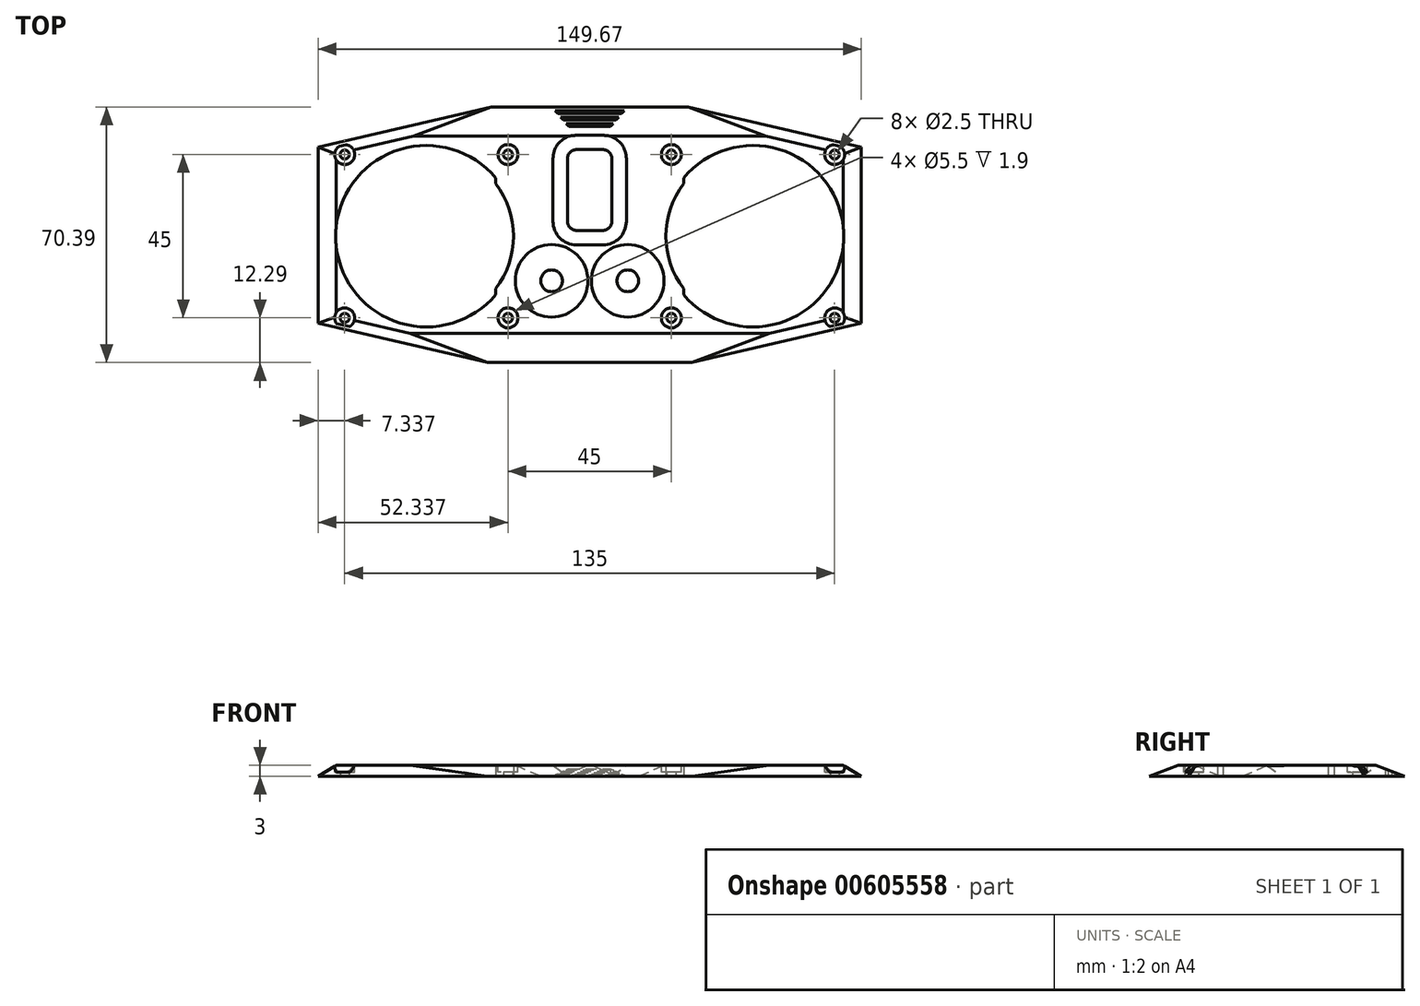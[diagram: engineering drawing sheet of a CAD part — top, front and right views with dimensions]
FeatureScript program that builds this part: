
annotation { "Feature Type Name" : "Feature", "Feature Type Description" : "" }
export const myFeature = defineFeature(function(context is Context, id is Id, definition is map)
    precondition{}
    {
        {
            var Q0;
            Q0=qCreatedBy(makeId("Top.planeOp"),FACE);
            var sketch = newSketch(context, id + "F0", { "sketchPlane" : qUnion([Q0])});
            skArc(sketch, "E0.0", {"start": v(-27.05, 29.93) * mm, "mid": v(-71.2, 13.86) * mm, "end": v(-27.05, -2.2) * mm});
            skArc(sketch, "E0.1", {"start": v(-27.05, -0.6) * mm, "mid": v(-22.2, 13.86) * mm, "end": v(-27.05, 28.32) * mm});
            skLineSegment(sketch, "E0.2", {"start": v(-27.05, -2.2) * mm, "end": v(-27.05, -0.6) * mm});
            skLineSegment(sketch, "E0.3", {"start": v(-27.05, 29.93) * mm, "end": v(-27.05, 28.32) * mm});
            skCircle(sketch, "E0.4", {"center": v(-23.7, 36.36) * mm, "radius": 1.25 * mm});
            skCircle(sketch, "E0.5", {"center": v(-68.7, 36.36) * mm, "radius": 1.25 * mm});
            skLineSegment(sketch, "E0.6", {"start": v(-77.2, 39.39) * mm, "end": v(-28.53, 50.62) * mm, "construction": true});
            skLineSegment(sketch, "E0.7", {"start": v(-77.2, 39.39) * mm, "end": v(-77.2, -45.78) * mm, "construction": true});
            skLineSegment(sketch, "E0.8", {"start": v(-28.53, 50.62) * mm, "end": v(26.12, 50.62) * mm, "construction": true});
            skLineSegment(sketch, "E0.9", {"start": v(74.8, 39.39) * mm, "end": v(26.12, 50.62) * mm, "construction": true});
            skLineSegment(sketch, "E0.10", {"start": v(-12.2, 50.26) * mm, "end": v(9.8, 50.26) * mm, "construction": true});
            skLineSegment(sketch, "E0.11", {"start": v(-11.4, 49.46) * mm, "end": v(9, 49.46) * mm, "construction": true});
            skLineSegment(sketch, "E0.12", {"start": v(8.3, 48.46) * mm, "end": v(-10.7, 48.46) * mm});
            skLineSegment(sketch, "E0.13", {"start": v(7.5, 47.66) * mm, "end": v(-9.9, 47.66) * mm});
            skLineSegment(sketch, "E0.14", {"start": v(6.8, 46.66) * mm, "end": v(-9.2, 46.66) * mm});
            skLineSegment(sketch, "E0.15", {"start": v(6, 45.86) * mm, "end": v(-8.4, 45.86) * mm});
            skLineSegment(sketch, "E0.16", {"start": v(5.3, 44.86) * mm, "end": v(-7.7, 44.86) * mm});
            skLineSegment(sketch, "E0.17", {"start": v(4.5, 44.06) * mm, "end": v(-6.9, 44.06) * mm});
            skLineSegment(sketch, "E0.18", {"start": v(-5.3, 35.25) * mm, "end": v(-5.3, 17.95) * mm, "construction": true});
            skLineSegment(sketch, "E0.19", {"start": v(2.4, 35.75) * mm, "end": v(-4.8, 35.75) * mm, "construction": true});
            skLineSegment(sketch, "E0.20", {"start": v(2.9, 35.25) * mm, "end": v(2.9, 17.95) * mm, "construction": true});
            skLineSegment(sketch, "E0.21", {"start": v(2.4, 17.45) * mm, "end": v(-4.8, 17.45) * mm, "construction": true});
            skArc(sketch, "E0.22", {"start": v(-4.8, 17.45) * mm, "mid": v(-5.16, 17.6) * mm, "end": v(-5.3, 17.95) * mm, "construction": true});
            skArc(sketch, "E0.23", {"start": v(2.9, 17.95) * mm, "mid": v(2.75, 17.6) * mm, "end": v(2.4, 17.45) * mm, "construction": true});
            skArc(sketch, "E0.24", {"start": v(2.4, 35.75) * mm, "mid": v(2.75, 35.6) * mm, "end": v(2.9, 35.25) * mm, "construction": true});
            skArc(sketch, "E0.25", {"start": v(-5.3, 35.25) * mm, "mid": v(-5.16, 35.6) * mm, "end": v(-4.8, 35.75) * mm, "construction": true});
            skCircle(sketch, "E0.26", {"center": v(21.3, 36.36) * mm, "radius": 1.25 * mm});
            skCircle(sketch, "E0.27", {"center": v(66.3, 36.36) * mm, "radius": 1.25 * mm});
            skCircle(sketch, "E0.28", {"center": v(66.3, -8.64) * mm, "radius": 1.25 * mm});
            skCircle(sketch, "E0.29", {"center": v(21.3, -8.64) * mm, "radius": 1.25 * mm});
            skArc(sketch, "E0.30", {"start": v(24.64, -2.2) * mm, "mid": v(68.8, 13.86) * mm, "end": v(24.64, 29.93) * mm});
            skArc(sketch, "E0.31", {"start": v(24.64, 28.32) * mm, "mid": v(19.8, 13.86) * mm, "end": v(24.64, -0.6) * mm});
            skLineSegment(sketch, "E0.32", {"start": v(74.8, -45.78) * mm, "end": v(74.8, 39.39) * mm, "construction": true});
            skLineSegment(sketch, "E0.33", {"start": v(24.64, -2.2) * mm, "end": v(24.64, -0.6) * mm});
            skLineSegment(sketch, "E0.34", {"start": v(24.64, 29.93) * mm, "end": v(24.64, 28.32) * mm});
            skLineSegment(sketch, "E0.35", {"start": v(13.5, 10.27) * mm, "end": v(5.1, 10.27) * mm, "construction": true});
            skLineSegment(sketch, "E0.36", {"start": v(13.5, 5.77) * mm, "end": v(13.5, 10.27) * mm, "construction": true});
            skLineSegment(sketch, "E0.37", {"start": v(18, 5.77) * mm, "end": v(13.5, 5.77) * mm, "construction": true});
            skLineSegment(sketch, "E0.38", {"start": v(18, -2.63) * mm, "end": v(18, 5.77) * mm, "construction": true});
            skLineSegment(sketch, "E0.39", {"start": v(13.5, -2.63) * mm, "end": v(18, -2.63) * mm, "construction": true});
            skLineSegment(sketch, "E0.40", {"start": v(13.5, -7.13) * mm, "end": v(13.5, -2.63) * mm, "construction": true});
            skLineSegment(sketch, "E0.41", {"start": v(13.5, -7.13) * mm, "end": v(5.1, -7.13) * mm, "construction": true});
            skLineSegment(sketch, "E0.42", {"start": v(5.1, -7.13) * mm, "end": v(5.1, -2.63) * mm, "construction": true});
            skLineSegment(sketch, "E0.43", {"start": v(0.6, -2.63) * mm, "end": v(5.1, -2.63) * mm, "construction": true});
            skLineSegment(sketch, "E0.44", {"start": v(0.6, -2.63) * mm, "end": v(0.6, 5.77) * mm, "construction": true});
            skLineSegment(sketch, "E0.45", {"start": v(5.1, 5.77) * mm, "end": v(0.6, 5.77) * mm, "construction": true});
            skLineSegment(sketch, "E0.46", {"start": v(5.1, 5.77) * mm, "end": v(5.1, 10.27) * mm, "construction": true});
            skLineSegment(sketch, "E0.47", {"start": v(-3, -2.63) * mm, "end": v(-3, 5.77) * mm, "construction": true});
            skLineSegment(sketch, "E0.48", {"start": v(-7.5, 5.77) * mm, "end": v(-3, 5.77) * mm, "construction": true});
            skLineSegment(sketch, "E0.49", {"start": v(-7.5, 5.77) * mm, "end": v(-7.5, 10.27) * mm, "construction": true});
            skLineSegment(sketch, "E0.50", {"start": v(-15.9, 10.27) * mm, "end": v(-7.5, 10.27) * mm, "construction": true});
            skLineSegment(sketch, "E0.51", {"start": v(-15.9, 5.77) * mm, "end": v(-15.9, 10.27) * mm, "construction": true});
            skLineSegment(sketch, "E0.52", {"start": v(-20.4, 5.77) * mm, "end": v(-15.9, 5.77) * mm, "construction": true});
            skLineSegment(sketch, "E0.53", {"start": v(-20.4, -2.63) * mm, "end": v(-20.4, 5.77) * mm, "construction": true});
            skLineSegment(sketch, "E0.54", {"start": v(-15.9, -2.63) * mm, "end": v(-20.4, -2.63) * mm, "construction": true});
            skLineSegment(sketch, "E0.55", {"start": v(-15.9, -7.13) * mm, "end": v(-15.9, -2.63) * mm, "construction": true});
            skLineSegment(sketch, "E0.56", {"start": v(-15.9, -7.13) * mm, "end": v(-7.5, -7.13) * mm, "construction": true});
            skLineSegment(sketch, "E0.57", {"start": v(-7.5, -7.13) * mm, "end": v(-7.5, -2.63) * mm, "construction": true});
            skLineSegment(sketch, "E0.58", {"start": v(-3, -2.63) * mm, "end": v(-7.5, -2.63) * mm, "construction": true});
            skCircle(sketch, "E0.59", {"center": v(-23.7, -8.64) * mm, "radius": 1.25 * mm});
            skCircle(sketch, "E0.60", {"center": v(-53.22, -28.82) * mm, "radius": 4.05 * mm, "construction": true});
            skCircle(sketch, "E0.61", {"center": v(-53.22, -42.82) * mm, "radius": 4.05 * mm, "construction": true});
            skLineSegment(sketch, "E0.62", {"start": v(-73.07, -50.7) * mm, "end": v(-43.77, -55.87) * mm, "construction": true});
            skArc(sketch, "E0.63", {"start": v(-77.2, -45.78) * mm, "mid": v(-76.03, -48.99) * mm, "end": v(-73.07, -50.7) * mm, "construction": true});
            skLineSegment(sketch, "E0.64", {"start": v(-43.77, -55.87) * mm, "end": v(41.36, -55.87) * mm, "construction": true});
            skLineSegment(sketch, "E0.65", {"start": v(41.36, -55.87) * mm, "end": v(70.67, -50.7) * mm, "construction": true});
            skCircle(sketch, "E0.66", {"center": v(53.62, -34.26) * mm, "radius": 16.25 * mm, "construction": true});
            skArc(sketch, "E0.67", {"start": v(70.67, -50.7) * mm, "mid": v(73.63, -48.99) * mm, "end": v(74.8, -45.78) * mm, "construction": true});
            skLineSegment(sketch, "E0.68", {"start": v(-29.45, -20.93) * mm, "end": v(27.05, -20.93) * mm});
            skLineSegment(sketch, "E0.69", {"start": v(27.05, -54.93) * mm, "end": v(27.05, -20.93) * mm, "construction": true});
            skLineSegment(sketch, "E0.70", {"start": v(-29.45, -54.93) * mm, "end": v(-29.45, -20.93) * mm, "construction": true});
            skLineSegment(sketch, "E0.71", {"start": v(-29.45, -54.93) * mm, "end": v(27.05, -54.93) * mm, "construction": true});
            skCircle(sketch, "E0.72", {"center": v(-68.7, -8.64) * mm, "radius": 1.25 * mm});
            skLineSegment(sketch, "E1", {"start": v(-1.2, 35.75) * mm, "end": v(-1.2, 17.45) * mm, "construction": true});
            skLineSegment(sketch, "E2", {"start": v(-5.3, 26.6) * mm, "end": v(2.9, 26.6) * mm, "construction": true});
            skLineSegment(sketch, "E3", {"start": v(-11.7, 10.27) * mm, "end": v(-11.7, -7.13) * mm, "construction": true});
            skLineSegment(sketch, "E4", {"start": v(-20.4, 1.57) * mm, "end": v(-3, 1.57) * mm, "construction": true});
            skLineSegment(sketch, "E5", {"start": v(9.3, 10.27) * mm, "end": v(9.3, -7.13) * mm, "construction": true});
            skLineSegment(sketch, "E6", {"start": v(0.6, 1.57) * mm, "end": v(18, 1.57) * mm, "construction": true});
            skCircle(sketch, "E7", {"center": v(-11.7, 1.57) * mm, "radius": 3 * mm});
            skCircle(sketch, "E8", {"center": v(9.3, 1.57) * mm, "radius": 3 * mm});
            skLineSegment(sketch, "E9", {"start": v(-12.2, 50.26) * mm, "end": v(-11.4, 49.46) * mm, "construction": true});
            skLineSegment(sketch, "E10", {"start": v(-10.7, 48.46) * mm, "end": v(-9.9, 47.66) * mm});
            skLineSegment(sketch, "E11", {"start": v(-9.2, 46.66) * mm, "end": v(-8.4, 45.86) * mm});
            skLineSegment(sketch, "E12", {"start": v(-7.7, 44.86) * mm, "end": v(-6.9, 44.06) * mm});
            skLineSegment(sketch, "E13", {"start": v(9.8, 50.26) * mm, "end": v(9, 49.46) * mm, "construction": true});
            skLineSegment(sketch, "E14", {"start": v(8.3, 48.46) * mm, "end": v(7.5, 47.66) * mm});
            skLineSegment(sketch, "E15", {"start": v(6.8, 46.66) * mm, "end": v(6, 45.86) * mm});
            skLineSegment(sketch, "E16", {"start": v(5.3, 44.86) * mm, "end": v(4.5, 44.06) * mm});
            skArc(sketch, "E17.0", {"start": v(4.9, 17.95) * mm, "mid": v(4.17, 16.19) * mm, "end": v(2.4, 15.45) * mm});
            skLineSegment(sketch, "E17.1", {"start": v(4.9, 35.25) * mm, "end": v(4.9, 17.95) * mm});
            skLineSegment(sketch, "E17.2", {"start": v(2.4, 15.45) * mm, "end": v(-4.8, 15.45) * mm});
            skArc(sketch, "E17.3", {"start": v(2.4, 37.75) * mm, "mid": v(4.17, 37.02) * mm, "end": v(4.9, 35.25) * mm});
            skArc(sketch, "E17.4", {"start": v(-4.8, 15.45) * mm, "mid": v(-6.57, 16.19) * mm, "end": v(-7.3, 17.95) * mm});
            skLineSegment(sketch, "E17.5", {"start": v(-7.3, 35.25) * mm, "end": v(-7.3, 17.95) * mm});
            skArc(sketch, "E17.6", {"start": v(-7.3, 35.25) * mm, "mid": v(-6.57, 37.02) * mm, "end": v(-4.8, 37.75) * mm});
            skLineSegment(sketch, "E17.7", {"start": v(2.4, 37.75) * mm, "end": v(-4.8, 37.75) * mm});
            skLineSegment(sketch, "E18.0", {"start": v(73.63, -45.78) * mm, "end": v(73.63, 38.46) * mm});
            skLineSegment(sketch, "E18.1", {"start": v(-76.04, 38.46) * mm, "end": v(-76.04, -45.78) * mm});
            skLineSegment(sketch, "E18.2", {"start": v(-76.04, 38.46) * mm, "end": v(-28.4, 49.46) * mm});
            skLineSegment(sketch, "E18.3", {"start": v(-28.4, 49.46) * mm, "end": v(26, 49.46) * mm});
            skLineSegment(sketch, "E18.4", {"start": v(73.63, 38.46) * mm, "end": v(26, 49.46) * mm});
            skLineSegment(sketch, "E19", {"start": v(-76.04, -10.17) * mm, "end": v(-44.15, -17.53) * mm});
            skLineSegment(sketch, "E20", {"start": v(-29.45, -20.93) * mm, "end": v(-44.15, -17.53) * mm});
            skLineSegment(sketch, "E21", {"start": v(27.05, -20.93) * mm, "end": v(73.63, -10.17) * mm});
            skSolve(sketch);
        }
        {
            var Q0;
            Q0=makeQuery(id+"F0.imprint","IMPRINT",FACE,{"disambiguationData":[TD([[makeQuery(id+"F0.imprint","IMPRINT",EDGE,{"derivedFrom":sQuery(id+"F0.wireOp",EDGE,"E0.0")}),-1.0]])]});
            extrude(context, id + "F1", {"entities" : qUnion([Q0]), "depth" : 3 * mm, "offsetDistance" : 25 * mm});
        }
        {
            var Q0;
            Q0=makeQuery(id+"F1.opExtrude","CAP_EDGE",EDGE,{"disambiguationData":[OSD([sQuery(id+"F0.wireOp",EDGE,"E8")])],"isStart":false});
            var Q1;
            Q1=makeQuery(id+"F1.opExtrude","CAP_EDGE",EDGE,{"disambiguationData":[OSD([sQuery(id+"F0.wireOp",EDGE,"E7")])],"isStart":false});
            chamfer(context, id + "F2", {"entities" : qUnion([Q0, Q1]), "chamferType" : ChamferType.TWO_OFFSETS, "width1" : 3 * mm, "oppositeDirection" : false, "width2" : 7 * mm, "tangentPropagation" : true});
        }
        {
            var Q0;
            Q0=makeQuery(id+"F1.opExtrude","CAP_EDGE",EDGE,{"disambiguationData":[OSD([sQuery(id+"F0.wireOp",EDGE,"E17.7")])],"isStart":false});
            var Q1;
            Q1=makeQuery(id+"F1.opExtrude","CAP_EDGE",EDGE,{"disambiguationData":[OSD([sQuery(id+"F0.wireOp",EDGE,"E17.5")])],"isStart":false});
            var Q2;
            Q2=makeQuery(id+"F1.opExtrude","CAP_EDGE",EDGE,{"disambiguationData":[OSD([sQuery(id+"F0.wireOp",EDGE,"E17.2")])],"isStart":false});
            var Q3;
            Q3=makeQuery(id+"F1.opExtrude","CAP_EDGE",EDGE,{"disambiguationData":[OSD([sQuery(id+"F0.wireOp",EDGE,"E17.4")])],"isStart":false});
            var Q4;
            Q4=makeQuery(id+"F1.opExtrude","CAP_EDGE",EDGE,{"disambiguationData":[OSD([sQuery(id+"F0.wireOp",EDGE,"E17.0")])],"isStart":false});
            var Q5;
            Q5=makeQuery(id+"F1.opExtrude","CAP_EDGE",EDGE,{"disambiguationData":[OSD([sQuery(id+"F0.wireOp",EDGE,"E17.1")])],"isStart":false});
            var Q6;
            Q6=makeQuery(id+"F1.opExtrude","CAP_EDGE",EDGE,{"disambiguationData":[OSD([sQuery(id+"F0.wireOp",EDGE,"E17.3")])],"isStart":false});
            var Q7;
            Q7=makeQuery(id+"F1.opExtrude","CAP_EDGE",EDGE,{"disambiguationData":[OSD([sQuery(id+"F0.wireOp",EDGE,"E17.6")])],"isStart":false});
            chamfer(context, id + "F3", {"entities" : qUnion([Q0, Q1, Q2, Q3, Q4, Q5, Q6, Q7]), "chamferType" : ChamferType.TWO_OFFSETS, "width1" : 3 * mm, "oppositeDirection" : false, "width2" : 4 * mm, "tangentPropagation" : true});
        }
        {
            var Q0;
            Q0=makeQuery(id+"F1.opExtrude","CAP_EDGE",EDGE,{"disambiguationData":[OSD([sQuery(id+"F0.wireOp",EDGE,"E18.3")])],"isStart":false});
            var Q1;
            Q1=makeQuery(id+"F1.opExtrude","CAP_EDGE",EDGE,{"disambiguationData":[OSD([sQuery(id+"F0.wireOp",EDGE,"E0.68")])],"isStart":false});
            chamfer(context, id + "F4", {"entities" : qUnion([Q0, Q1]), "chamferType" : ChamferType.TWO_OFFSETS, "width1" : 3 * mm, "oppositeDirection" : false, "width2" : 8 * mm, "tangentPropagation" : true});
        }
        {
            var Q0;
            Q0=makeQuery(id+"F1.opExtrude","CAP_EDGE",EDGE,{"disambiguationData":[OSD([sQuery(id+"F0.wireOp",EDGE,"E18.1")])],"isStart":false});
            var Q1;
            Q1=makeQuery(id+"F1.opExtrude","CAP_EDGE",EDGE,{"disambiguationData":[OSD([sQuery(id+"F0.wireOp",EDGE,"E18.0")])],"isStart":false});
            chamfer(context, id + "F5", {"entities" : qUnion([Q0, Q1]), "chamferType" : ChamferType.TWO_OFFSETS, "width1" : 5 * mm, "oppositeDirection" : false, "width2" : 3 * mm, "tangentPropagation" : true});
        }
        {
            var Q0;
            Q0=makeQuery(id+"F1.opExtrude","CAP_EDGE",EDGE,{"disambiguationData":[OSD([sQuery(id+"F0.wireOp",EDGE,"E19"),sQuery(id+"F0.wireOp",EDGE,"E20")])],"isStart":false});
            var Q1;
            Q1=makeQuery(id+"F1.opExtrude","CAP_EDGE",EDGE,{"disambiguationData":[OSD([sQuery(id+"F0.wireOp",EDGE,"E18.2")])],"isStart":false});
            var Q2;
            Q2=makeQuery(id+"F1.opExtrude","CAP_EDGE",EDGE,{"disambiguationData":[OSD([sQuery(id+"F0.wireOp",EDGE,"E21")])],"isStart":false});
            var Q3;
            Q3=makeQuery(id+"F1.opExtrude","CAP_EDGE",EDGE,{"disambiguationData":[OSD([sQuery(id+"F0.wireOp",EDGE,"E18.4")])],"isStart":false});
            chamfer(context, id + "F6", {"entities" : qUnion([Q0, Q1, Q2, Q3]), "chamferType" : ChamferType.TWO_OFFSETS, "width1" : 3 * mm, "oppositeDirection" : false, "width2" : 3 * mm, "tangentPropagation" : true});
        }
        {
            var Q0;
            Q0=makeQuery(id+"F1.opExtrude","CAP_FACE",FACE,{"disambiguationData":[OSD([sQuery(id+"F0.wireOp",EDGE,"E0.0"),sQuery(id+"F0.wireOp",EDGE,"E0.1"),sQuery(id+"F0.wireOp",EDGE,"E0.2"),sQuery(id+"F0.wireOp",EDGE,"E0.3"),sQuery(id+"F0.wireOp",EDGE,"E0.4"),sQuery(id+"F0.wireOp",EDGE,"E0.5"),sQuery(id+"F0.wireOp",EDGE,"E0.12"),sQuery(id+"F0.wireOp",EDGE,"E0.13"),sQuery(id+"F0.wireOp",EDGE,"E0.14"),sQuery(id+"F0.wireOp",EDGE,"E0.15"),sQuery(id+"F0.wireOp",EDGE,"E0.16"),sQuery(id+"F0.wireOp",EDGE,"E0.17"),sQuery(id+"F0.wireOp",EDGE,"E0.26"),sQuery(id+"F0.wireOp",EDGE,"E0.27"),sQuery(id+"F0.wireOp",EDGE,"E0.28"),sQuery(id+"F0.wireOp",EDGE,"E0.29"),sQuery(id+"F0.wireOp",EDGE,"E0.30"),sQuery(id+"F0.wireOp",EDGE,"E0.31"),sQuery(id+"F0.wireOp",EDGE,"E0.33"),sQuery(id+"F0.wireOp",EDGE,"E0.34"),sQuery(id+"F0.wireOp",EDGE,"E0.59"),sQuery(id+"F0.wireOp",EDGE,"E0.68"),sQuery(id+"F0.wireOp",EDGE,"E0.72"),sQuery(id+"F0.wireOp",EDGE,"E7"),sQuery(id+"F0.wireOp",EDGE,"E8"),sQuery(id+"F0.wireOp",EDGE,"E10"),sQuery(id+"F0.wireOp",EDGE,"E11"),sQuery(id+"F0.wireOp",EDGE,"E12"),sQuery(id+"F0.wireOp",EDGE,"E14"),sQuery(id+"F0.wireOp",EDGE,"E15"),sQuery(id+"F0.wireOp",EDGE,"E16"),sQuery(id+"F0.wireOp",EDGE,"E17.0"),sQuery(id+"F0.wireOp",EDGE,"E17.1"),sQuery(id+"F0.wireOp",EDGE,"E17.2"),sQuery(id+"F0.wireOp",EDGE,"E17.3"),sQuery(id+"F0.wireOp",EDGE,"E17.4"),sQuery(id+"F0.wireOp",EDGE,"E17.5"),sQuery(id+"F0.wireOp",EDGE,"E17.6"),sQuery(id+"F0.wireOp",EDGE,"E17.7"),sQuery(id+"F0.wireOp",EDGE,"E18.0"),sQuery(id+"F0.wireOp",EDGE,"E18.1"),sQuery(id+"F0.wireOp",EDGE,"E18.2"),sQuery(id+"F0.wireOp",EDGE,"E18.3"),sQuery(id+"F0.wireOp",EDGE,"E18.4"),sQuery(id+"F0.wireOp",EDGE,"E19"),sQuery(id+"F0.wireOp",EDGE,"E20"),sQuery(id+"F0.wireOp",EDGE,"E21")])],"isStart":false});
            var sketch = newSketch(context, id + "F7", { "sketchPlane" : qUnion([Q0])});
            skCircle(sketch, "E22.0", {"center": v(-23.7, 36.36) * mm, "radius": 1.25 * mm});
            skCircle(sketch, "E22.1", {"center": v(21.3, 36.36) * mm, "radius": 1.25 * mm});
            skCircle(sketch, "E22.2", {"center": v(66.3, 36.36) * mm, "radius": 1.25 * mm});
            skCircle(sketch, "E22.3", {"center": v(66.3, -8.64) * mm, "radius": 1.25 * mm});
            skCircle(sketch, "E22.4", {"center": v(21.3, -8.64) * mm, "radius": 1.25 * mm});
            skCircle(sketch, "E22.5", {"center": v(-23.7, -8.64) * mm, "radius": 1.25 * mm});
            skCircle(sketch, "E22.6", {"center": v(-68.7, -8.64) * mm, "radius": 1.25 * mm});
            skCircle(sketch, "E22.7", {"center": v(-68.7, 36.36) * mm, "radius": 1.25 * mm});
            skCircle(sketch, "E23", {"center": v(-68.7, 36.36) * mm, "radius": 2.75 * mm});
            skCircle(sketch, "E24", {"center": v(-23.7, 36.36) * mm, "radius": 2.75 * mm});
            skCircle(sketch, "E25", {"center": v(21.3, 36.36) * mm, "radius": 2.75 * mm});
            skCircle(sketch, "E26", {"center": v(66.3, 36.36) * mm, "radius": 2.75 * mm});
            skCircle(sketch, "E27", {"center": v(66.3, -8.64) * mm, "radius": 2.75 * mm});
            skCircle(sketch, "E28", {"center": v(21.3, -8.64) * mm, "radius": 2.75 * mm});
            skCircle(sketch, "E29", {"center": v(-23.7, -8.64) * mm, "radius": 2.75 * mm});
            skCircle(sketch, "E30", {"center": v(-68.7, -8.64) * mm, "radius": 2.75 * mm});
            skSolve(sketch);
        }
        {
            var Q0;
            Q0 = qSketchRegion(id + "F7", true);
            extrude(context, id + "F8", {"entities" : qUnion([Q0]), "operationType" : NewBodyOperationType.REMOVE, "oppositeDirection" : true, "depth" : 1.9 * mm, "offsetDistance" : 25 * mm});
        }
    });
